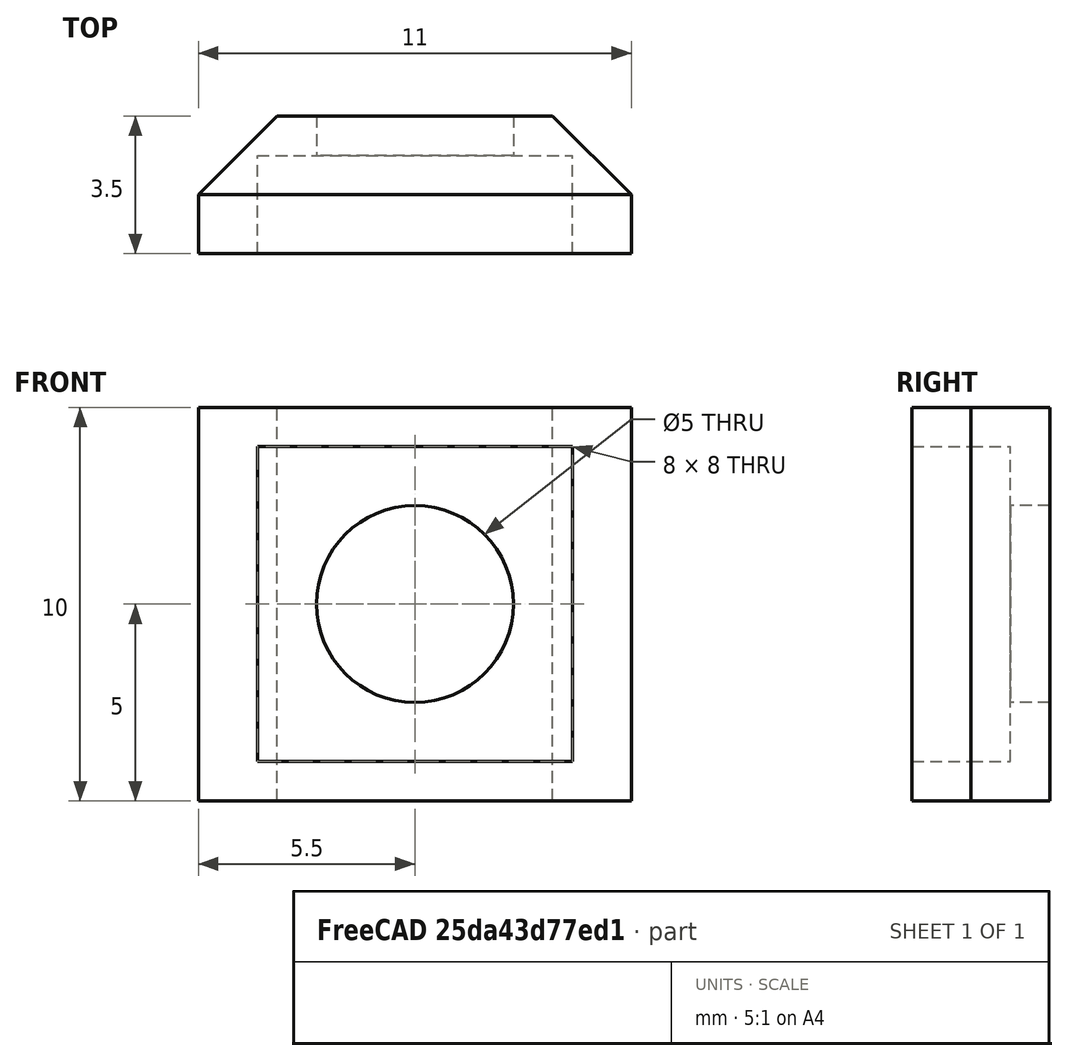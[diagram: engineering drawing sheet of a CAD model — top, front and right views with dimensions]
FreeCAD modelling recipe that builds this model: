
FCSTD DOCUMENT  (FreeCAD 0.19R24276 (Git))
Label: T-hold_midi_005
License: All rights reserved
LicenseURL: http://en.wikipedia.org/wiki/All_rights_reserved
objects: Part::Cut×5, Part::Box×3, Part::Cylinder×3, Part::Wedge×1, Part::Compound×1, Mesh::Feature×1
note: 13 computed .brp shape members not serialized (recipe doc carries the construction recipe); baked Part::Feature solids carry a one-line shape summary decoded from their .brp

FEATURE [Part::Wedge] Wedge  label="Klín"
  AttacherType = Attacher::AttachEngine3D
  X2max = 9
  X2min = 2
  Xmax = 11
  Xmin = 0
  Ymax = 2
  Ymin = 0
  Z2max = 10
  Z2min = 0
  Zmax = 10
  Zmin = 0
FEATURE [Part::Box] Box  label="Krychle"
  AttacherType = Attacher::AttachEngine3D
  Height = 10
  Length = 11
  Placement = pos=(0,-1.5,0) rot=(0,0,1;0rad)
  Width = 1.5
FEATURE [Part::Box] Box001  label="Krychle001"
  AttacherType = Attacher::AttachEngine3D
  Height = 8
  Length = 8
  Placement = pos=(1.5,-1.5,1) rot=(0,0,1;0rad)
  Width = 2.5
FEATURE [Part::Box] Box002  label="Krychle002"
  AttacherType = Attacher::AttachEngine3D
  Height = 8
  Length = 8
  Placement = pos=(1.5,-1.5,1) rot=(0,0,1;0rad)
  Width = 2.5
FEATURE [Part::Cut] Cut
  Base = -> Wedge
  Tool = -> Box001
FEATURE [Part::Cut] Cut001
  Base = -> Box
  Tool = -> Box002
FEATURE [Part::Cylinder] Cylinder  label="Válec"
  Angle = 360
  AttacherType = Attacher::AttachEngine3D
  Height = 10
  Placement = pos=(5.5,5,5) rot=(1,0,0;1.5708rad)
  Radius = 2.5
FEATURE [Part::Cylinder] Cylinder001  label="Válec001"
  Angle = 360
  AttacherType = Attacher::AttachEngine3D
  Height = 10
  Placement = pos=(5.5,5,5) rot=(1,0,0;1.5708rad)
  Radius = 2.5
FEATURE [Part::Cut] Cut002
  Base = -> Cut001
  Tool = -> Cylinder
FEATURE [Part::Cut] Cut003
  Base = -> Cut002
  Tool = -> Cylinder001
FEATURE [Part::Compound] Compound  label="teckovka"
  Links = -> [Cut,Cut003]
FEATURE [Part::Cylinder] Cylinder002  label="Válec002"
  Angle = 360
  AttacherType = Attacher::AttachEngine3D
  Height = 10
  Placement = pos=(5.5,5,5) rot=(1,0,0;1.5708rad)
  Radius = 2.5
FEATURE [Part::Cut] Cut004  label="T-hold_midi"
  Base = -> Compound
  Tool = -> Cylinder002
FEATURE [Mesh::Feature] Mesh  label="T-hold_midi (Meshed)"
